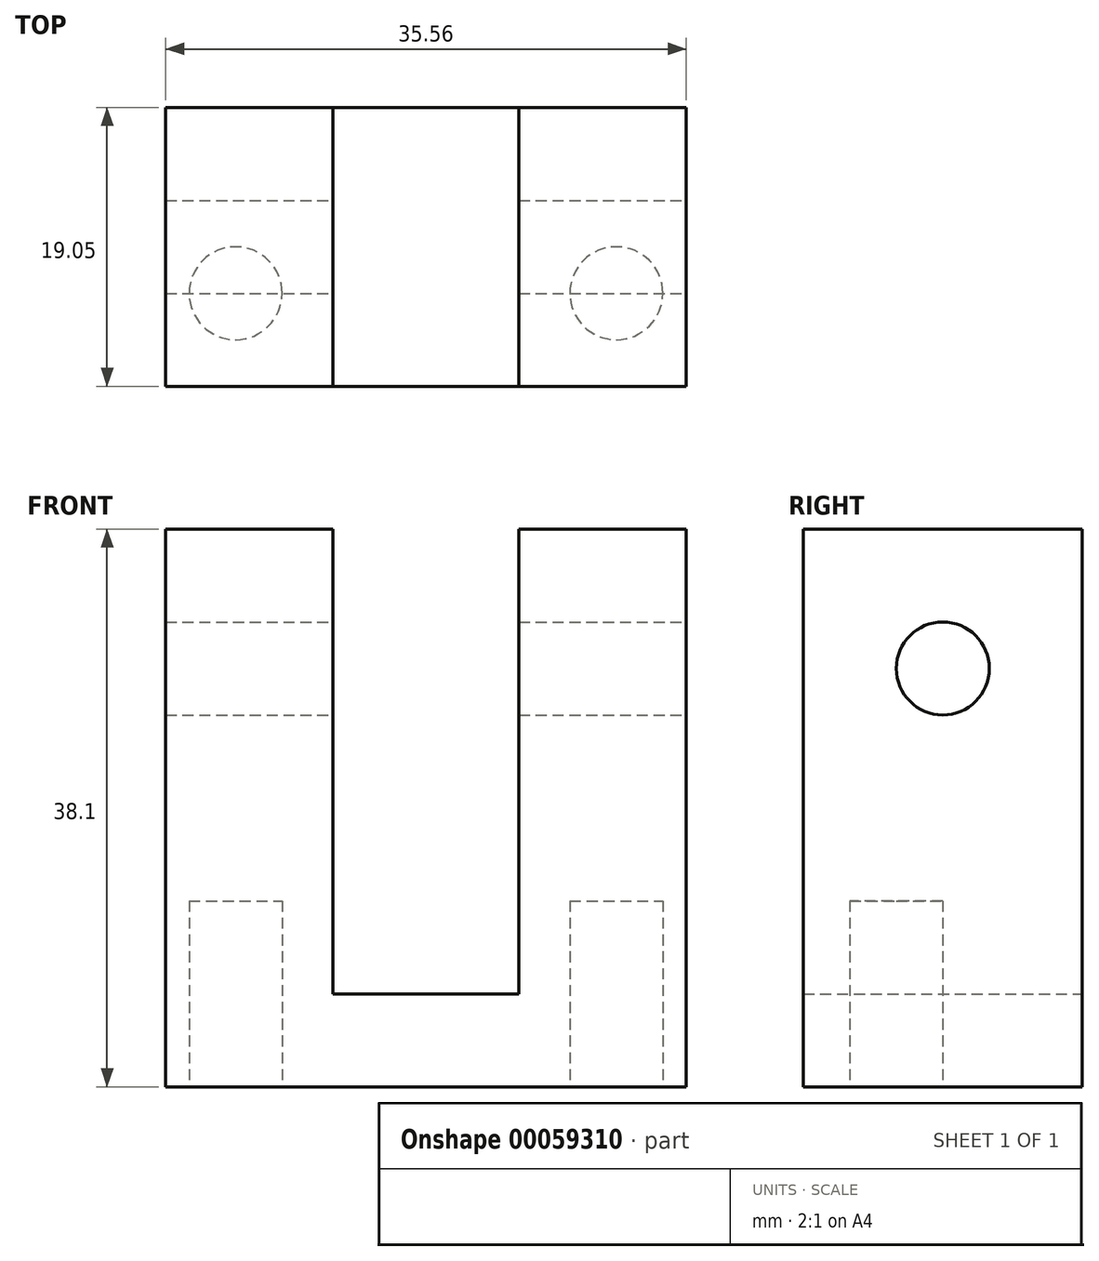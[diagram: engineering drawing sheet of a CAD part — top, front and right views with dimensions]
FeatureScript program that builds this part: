
annotation { "Feature Type Name" : "Feature", "Feature Type Description" : "" }
export const myFeature = defineFeature(function(context is Context, id is Id, definition is map)
    precondition{}
    {
        {
            var Q0;
            Q0=qCreatedBy(makeId("Front.planeOp"),FACE);
            var sketch = newSketch(context, id + "F0", { "sketchPlane" : qUnion([Q0])});
            skLineSegment(sketch, "E0", {"start": v(0, 0) * mm, "end": v(35.56, 0) * mm});
            skLineSegment(sketch, "E1", {"start": v(35.56, 0) * mm, "end": v(35.56, 38.1) * mm});
            skLineSegment(sketch, "E2", {"start": v(35.56, 38.1) * mm, "end": v(24.13, 38.1) * mm});
            skLineSegment(sketch, "E3", {"start": v(24.13, 38.1) * mm, "end": v(24.13, 6.35) * mm});
            skLineSegment(sketch, "E4", {"start": v(24.13, 6.35) * mm, "end": v(11.43, 6.35) * mm});
            skLineSegment(sketch, "E5", {"start": v(11.43, 6.35) * mm, "end": v(11.43, 38.1) * mm});
            skLineSegment(sketch, "E6", {"start": v(11.43, 38.1) * mm, "end": v(0, 38.1) * mm});
            skLineSegment(sketch, "E7", {"start": v(0, 38.1) * mm, "end": v(0, 0) * mm});
            skSolve(sketch);
        }
        {
            var Q0;
            Q0=makeQuery(id+"F0.imprint","IMPRINT",FACE,{"disambiguationData":[TD([[makeQuery(id+"F0.imprint","IMPRINT",EDGE,{"derivedFrom":sQuery(id+"F0.wireOp",EDGE,"E0")}),1.0]])]});
            extrude(context, id + "F1", {"entities" : qUnion([Q0]), "depth" : 19.05 * mm});
        }
        {
            var Q0;
            Q0=makeQuery(id+"F1.opExtrude","SWEPT_FACE",FACE,{"disambiguationData":[OSD([sQuery(id+"F0.wireOp",EDGE,"E1")])]});
            var sketch = newSketch(context, id + "F2", { "sketchPlane" : qUnion([Q0])});
            skCircle(sketch, "E8", {"center": v(-9.53, 28.58) * mm, "radius": 3.18 * mm});
            skSolve(sketch);
        }
        {
            var Q0;
            Q0=makeQuery(id+"F2.imprint","IMPRINT",FACE,{"disambiguationData":[TD([[makeQuery(id+"F2.imprint","IMPRINT",EDGE,{"derivedFrom":sQuery(id+"F2.wireOp",EDGE,"E8")}),1.0]])]});
            extrude(context, id + "F3", {"entities" : qUnion([Q0]), "operationType" : NewBodyOperationType.REMOVE, "oppositeDirection" : true, "depth" : 508 * mm});
        }
        {
            var Q0;
            Q0=makeQuery(id+"F1.opExtrude","SWEPT_FACE",FACE,{"disambiguationData":[OSD([sQuery(id+"F0.wireOp",EDGE,"E0")])]});
            var sketch = newSketch(context, id + "F4", { "sketchPlane" : qUnion([Q0])});
            skCircle(sketch, "E9", {"center": v(4.78, 12.7) * mm, "radius": 3.18 * mm});
            skCircle(sketch, "E10", {"center": v(30.78, 12.7) * mm, "radius": 3.18 * mm});
            skSolve(sketch);
        }
        {
            var Q0;
            Q0=makeQuery(id+"F4.imprint","IMPRINT",FACE,{"disambiguationData":[TD([[makeQuery(id+"F4.imprint","IMPRINT",EDGE,{"derivedFrom":sQuery(id+"F4.wireOp",EDGE,"E9")}),1.0]])]});
            var Q1;
            Q1=makeQuery(id+"F4.imprint","IMPRINT",FACE,{"disambiguationData":[TD([[makeQuery(id+"F4.imprint","IMPRINT",EDGE,{"derivedFrom":sQuery(id+"F4.wireOp",EDGE,"E10")}),1.0]])]});
            extrude(context, id + "F5", {"entities" : qUnion([Q0, Q1]), "operationType" : NewBodyOperationType.REMOVE, "oppositeDirection" : true, "depth" : 12.7 * mm});
        }
    });
